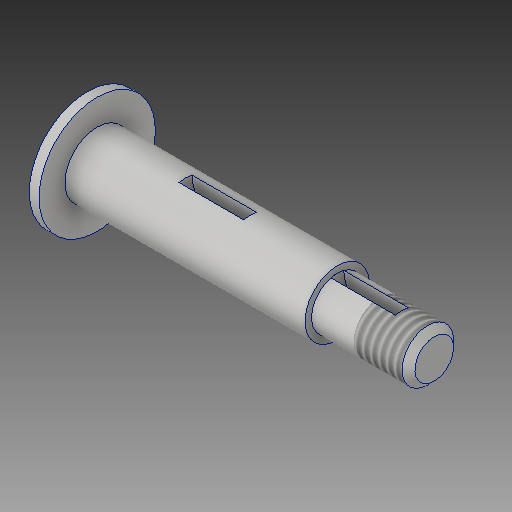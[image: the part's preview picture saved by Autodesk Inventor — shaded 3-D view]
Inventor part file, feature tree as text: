
AUTODESK INVENTOR PART (.ipt)
format: ipt  version: 2020 (Build 240168000, 168)  size: 157,184 bytes
history: native  units: in
note: dims shown in document units (in); Inventor stores cm internally (conversion verified against a paired STEP export)
features: sketch x2, revolve x1, extrude x1, chamfer x1, thread x1
ambient origin geometry x8: Origin, YZ Plane, XZ Plane, XY Plane, X Axis, Y Axis, Z Axis, Center Point
bodies: Solid1 (feature_tree)
feature tree (6):
  revolve  "Revolution1"  [1 undecoded]
  extrude  "Extrusion1"  Depth=0.125in
  chamfer  "Chamfer1"  [1 undecoded]
  thread  "Thread1"  [1 undecoded]
  sketch  "Sketch1"  dims[d4=0.6238in d6=0.9375in]
  sketch  "Sketch2"  dims[d8=2.3225in d9=0.4985in d10=0.0in d16=0.0938in d17=0.0938in d18=1.125in d19=90.0deg d20=1.1562in d21=0.3125in d22=0.625in d23=0.0in d24=0.0in d25=0.125in d26=0.0in d27=0.0625in d28=0.125in d29=45.0deg d30=0.4688in d31=0.0in]
note: 3 required parameter values undecoded (feature->parameter linkage not recoverable at this tier; creation-order binding heuristic only, values carry confidence <= 0.55)